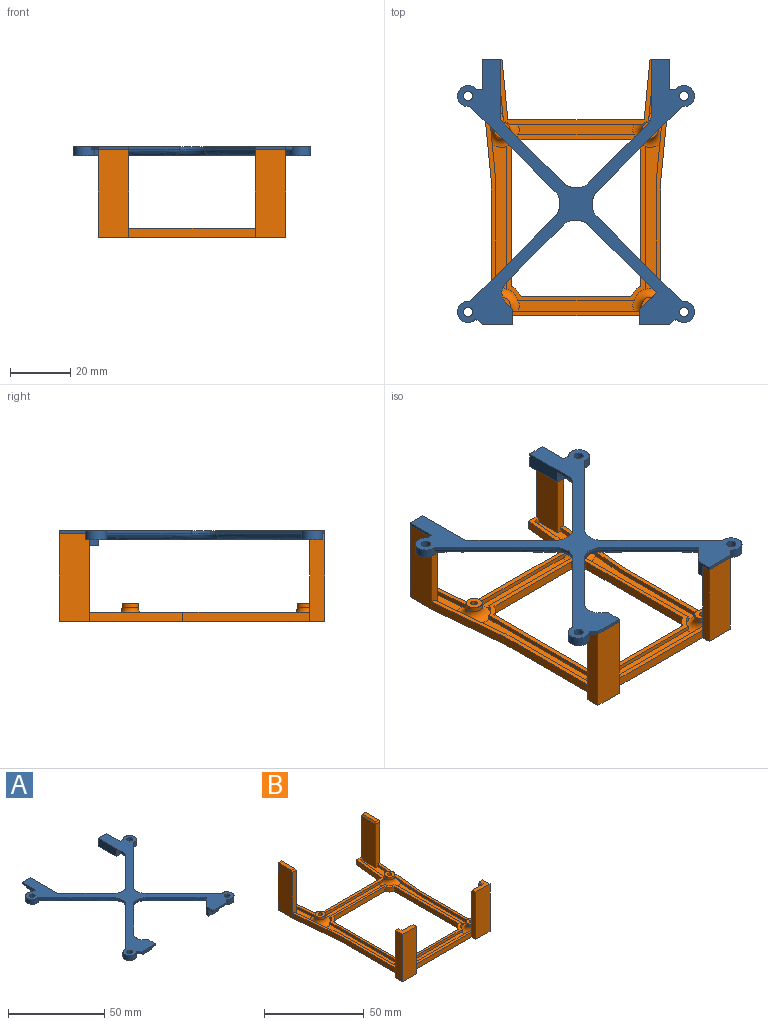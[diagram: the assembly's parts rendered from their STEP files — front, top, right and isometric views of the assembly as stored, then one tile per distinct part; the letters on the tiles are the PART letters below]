
ASSEMBLY  parts=2 mates=1
PART A: 84 faces, bbox 79.2x88.7x5.7 mm
  f0: plane 18.25x11.25mm, normal (0,0,-1), area 73.6mm2, adj f8,f9,f12,f35,f42,f60,f80
  f1: plane 14.31x14.31mm, normal (0,0,-1), area 66.3mm2, adj f6,f40,f43,f65,f66,f75,f78,f83
  f2: plane 15.43x14.79mm, normal (0,0,-1), area 66.3mm2, adj f13,f14,f15,f41,f58,f68,f69,f70
  f3: plane 11.32x11.32mm, normal (0,0,-1), area 54.9mm2, adj f71,f74,f79,f82
  f4: plane 14.25x14.25mm, normal (0,0,-1), area 83.3mm2, adj f23,f25,f26,f44,f62,f63,f73
  f5: plane 10x4mm, normal (1,0,0), area 40mm2, adj f6,f18,f55,f67
  f6: plane 5.07x5mm, normal (0,1,0), area 18.2mm2, adj f1,f5,f40,f45,f54,f55,f65,f67
  f7: plane 10x4mm, normal (-1,0,0), area 40mm2, adj f24,f25,f53,f64
  f8: plane 2.09x2.09mm, normal (0.71,-0.71,0), area 5.9mm2, adj f0,f9,f11,f51
  f9: plane 2.22x2.22mm, normal (-0.71,-0.71,0), area 6.3mm2, adj f0,f8,f12,f51
  f10: plane 7x4mm, normal (0,-1,0), area 28mm2, adj f11,f36,f51,f61
  f11: plane 4x2mm, normal (1,0,0), area 8mm2, adj f8,f10,f51,f60,f61
  f12: cylinder r=3.5mm len=7mm, axis (0,0,-1), area 52.2mm2, adj f0,f9,f37,f45,f50,f51,f80
  f13: plane 2.22x2.22mm, normal (0.71,-0.71,0), area 6.3mm2, adj f2,f14,f15,f48
  f14: plane 2.09x2.09mm, normal (-0.71,-0.71,0), area 5.9mm2, adj f2,f13,f16,f48
  f15: cylinder r=3.5mm len=7mm, axis (0,0,-1), area 52.2mm2, adj f2,f13,f29,f45,f46,f48,f69
  f16: plane 4x2mm, normal (-1,0,0), area 8mm2, adj f14,f17,f48,f58,f59
  f17: plane 7x4mm, normal (0,-1,0), area 28mm2, adj f16,f30,f48,f59
  f18: plane 6x5mm, normal (0,1,0), area 18mm2, adj f5,f19,f45,f54,f55,f67
  f19: plane 18.1x5mm, normal (-1,0,0), area 70.1mm2, adj f18,f45,f56,f66,f67,f75
  f20: plane 19.29x19.29mm, normal (-0.71,0.71,0), area 27.3mm2, adj f21,f45,f56,f81
  f21: cylinder r=6mm len=8.49mm, axis (0,0,-1), area 9.4mm2, adj f20,f22,f45,f79
  f22: plane 20.76x20.76mm, normal (0.71,0.71,0), area 29.4mm2, adj f21,f23,f45,f76
  f23: plane 23.69x5.69mm, normal (1,0,0), area 88.1mm2, adj f4,f22,f24,f45,f63,f64,f76
  f24: plane 6x5mm, normal (0,1,0), area 18mm2, adj f7,f23,f45,f52,f53,f64
  f25: plane 5.07x5mm, normal (0,1,0), area 18.2mm2, adj f4,f7,f26,f45,f52,f53,f62,f64
  f26: cylinder r=3.5mm len=7mm, axis (0,0,-1), area 46.1mm2, adj f4,f25,f27,f45,f73
  f27: plane 28.06x28.06mm, normal (-0.71,-0.71,0), area 39.7mm2, adj f26,f28,f45,f73
  f28: cylinder r=6mm len=8.49mm, axis (0,0,-1), area 9.4mm2, adj f27,f29,f45,f71
  f29: plane 28.06x28.06mm, normal (-0.71,0.71,0), area 39.7mm2, adj f15,f28,f45,f69
  f30: plane 5x5mm, normal (1,0,0), area 13mm2, adj f17,f31,f45,f47,f48,f58,f59
  f31: plane 2.05x2.05mm, normal (0.71,0.71,0), area 2.9mm2, adj f30,f45,f57,f68
  f32: plane 18.81x18.81mm, normal (0.71,-0.71,0), area 26.6mm2, adj f33,f45,f57,f72
  f33: cylinder r=6mm len=8.49mm, axis (0,0,-1), area 9.4mm2, adj f32,f34,f45,f74
  f34: plane 22.34x22.34mm, normal (-0.71,-0.71,0), area 31.6mm2, adj f33,f35,f45,f77
  f35: plane 7.33x7.33mm, normal (-0.71,0.71,0), area 24.8mm2, adj f0,f34,f36,f45,f77
  f36: plane 5x5mm, normal (-1,0,0), area 13mm2, adj f10,f35,f45,f49,f51,f60,f61
  f37: plane 28.06x28.06mm, normal (0.71,0.71,0), area 39.7mm2, adj f12,f38,f45,f80
  f38: cylinder r=6mm len=8.49mm, axis (0,0,-1), area 9.4mm2, adj f37,f39,f45,f82
  f39: plane 28.06x28.06mm, normal (0.71,-0.71,0), area 39.7mm2, adj f38,f40,f45,f83
  f40: cylinder r=3.5mm len=7mm, axis (0,0,-1), area 46.1mm2, adj f1,f6,f39,f45,f83
  f41: cylinder r=1.5mm len=3mm, axis (0,0,-1), area 28.3mm2, adj f2,f45
  f42: cylinder r=1.5mm len=3mm, axis (0,0,-1), area 28.3mm2, adj f0,f45
  f43: cylinder r=1.5mm len=3mm, axis (0,0,-1), area 28.3mm2, adj f1,f45
  f44: cylinder r=1.5mm len=3mm, axis (0,0,-1), area 28.3mm2, adj f4,f45
  f45: plane 88x78.5mm, normal (0,0,1), area 1294.3mm2, adj f6,f12,f15,f18,f19,f20,f21,f22
  f46: plane 2.14x1.92mm, normal (-0.67,-0.75,0), area 2.9mm2, adj f15,f45,f47,f48
  f47: plane 10x1mm, normal (0,-1,0), area 10mm2, adj f30,f45,f46,f48
  f48: plane 12.14x7.09mm, normal (0,0,-1), area 46.9mm2, adj f13,f14,f15,f16,f17,f30,f46,f47
  f49: plane 10x1mm, normal (0,-1,0), area 10mm2, adj f36,f45,f50,f51
  f50: plane 2.14x1.92mm, normal (0.67,-0.75,0), area 2.9mm2, adj f12,f45,f49,f51
  f51: plane 12.14x7.09mm, normal (0,0,-1), area 46.9mm2, adj f8,f9,f10,f11,f12,f36,f49,f50
  f52: plane 10x1mm, normal (-1,0,0), area 10mm2, adj f24,f25,f45,f53
  f53: plane 10x3mm, normal (0,0,-1), area 30mm2, adj f7,f24,f25,f52
  f54: plane 10x1mm, normal (1,0,0), area 10mm2, adj f6,f18,f45,f55
  f55: plane 10x3mm, normal (0,0,-1), area 30mm2, adj f5,f6,f18,f54
  f56: cylinder r=5mm len=3.54mm, axis (0,0,1), area 3.9mm2, adj f19,f20,f45,f78
  f57: cylinder r=5mm len=7.07mm, axis (0,0,1), area 7.9mm2, adj f31,f32,f45,f70
  f58: plane 7.69x4.69mm, normal (0,1,0), area 15.6mm2, adj f2,f16,f30,f59,f68
  f59: plane 7x2mm, normal (0,0,-1), area 14mm2, adj f16,f17,f30,f58
  f60: plane 7x2mm, normal (0,1,0), area 14mm2, adj f0,f11,f36,f61
  f61: plane 7x2mm, normal (0,0,-1), area 14mm2, adj f10,f11,f36,f60
  f62: plane 3x2mm, normal (-1,0,0), area 6mm2, adj f4,f25,f63,f64
  f63: plane 6x2mm, normal (0,-1,0), area 12mm2, adj f4,f23,f62,f64
  f64: plane 13x6mm, normal (0,0,-1), area 48mm2, adj f7,f23,f24,f25,f62,f63
  f65: plane 3x2mm, normal (1,0,0), area 6mm2, adj f1,f6,f66,f67
  f66: plane 6.33x4.33mm, normal (0,-1,0), area 13.1mm2, adj f1,f19,f65,f67,f75
  f67: plane 13x6mm, normal (0,0,-1), area 48mm2, adj f5,f6,f18,f19,f65,f66
  f68: bspline ~3.57x3.57mm, area 5.7mm2, adj f2,f31,f58,f70
  f69: bspline ~30.88x30.88mm, area 119.2mm2, adj f2,f15,f29,f71,f72
  f70: bspline ~9.9x3.65mm, area 27.5mm2, adj f2,f57,f68,f72
  f71: bspline ~11.31x3.97mm, area 32.3mm2, adj f3,f28,f69,f73
  f72: bspline ~20.22x20.22mm, area 80.5mm2, adj f32,f69,f70,f74
  f73: bspline ~30.88x30.88mm, area 119.2mm2, adj f4,f26,f27,f71,f76
  f74: bspline ~11.31x3.97mm, area 32.3mm2, adj f3,f33,f72,f77
  f75: bspline ~5.36x2mm, area 15.4mm2, adj f1,f19,f66,f78
  f76: bspline ~23.21x23.21mm, area 85.8mm2, adj f22,f23,f73,f79
  f77: bspline ~24.87x24.87mm, area 95.6mm2, adj f34,f35,f74,f80
  f78: bspline ~4.95x3.46mm, area 13.8mm2, adj f1,f56,f75,f81
  f79: bspline ~11.31x3.97mm, area 32.3mm2, adj f3,f21,f76,f81
  f80: bspline ~30.88x30.88mm, area 119.2mm2, adj f0,f12,f37,f77,f82
  f81: bspline ~20.9x20.9mm, area 82.6mm2, adj f20,f78,f79,f83
  f82: bspline ~11.31x3.97mm, area 32.3mm2, adj f3,f38,f80,f83
  f83: bspline ~30.88x30.88mm, area 119.2mm2, adj f1,f39,f40,f81,f82
PART B: 100 faces, bbox 66x90.1x29.1 mm
  f0: plane 74.5x4.5mm, normal (0,0,1), area 108.5mm2, adj f5,f6,f15,f16,f38,f39,f66,f88
  f1: plane 18.04x5.21mm, normal (0,0,1), area 58.8mm2, adj f18,f66,f67,f77,f90,f91
  f2: plane 45x1.5mm, normal (0,0,1), area 67.4mm2, adj f4,f6,f33,f64,f65,f79,f85,f87
  f3: plane 56x21.5mm, normal (0,0,1), area 136.1mm2, adj f8,f17,f18,f19,f41,f42,f43,f44
  f4: plane 1.2x1.05mm, normal (1,0,0), area 0.7mm2, adj f2,f6,f87
  f5: plane 1.62x1.43mm, normal (0,-1,0), area 1.5mm2, adj f0,f6,f15,f88
  f6: torus R=5.68mm, axis (0,0,1), area 65.8mm2, adj f0,f2,f4,f5,f10,f13,f15,f16
  f7: plane 74.5x4.5mm, normal (0,0,1), area 108.5mm2, adj f9,f20,f21,f47,f48,f63,f79,f82
  f8: plane 2.14x1.5mm, normal (0,-1,0), area 3.2mm2, adj f3,f12,f19,f81
  f9: plane 30.91x2.99mm, normal (1,0.1,0), area 43.4mm2, adj f7,f12,f14,f21,f78,f82
  f10: plane 48.03x4.73mm, normal (0,0,1), area 171.4mm2, adj f6,f16,f59,f66,f77
  f11: plane 38.38x3.5mm, normal (0,0,1), area 132.5mm2, adj f17,f57,f77,f78
  f12: plane 18.04x5.21mm, normal (0,0,1), area 58.8mm2, adj f8,f9,f19,f78,f81,f82
  f13: plane 38.38x3.5mm, normal (0,0,1), area 132.5mm2, adj f6,f61,f65,f79
  f14: plane 48.03x4.73mm, normal (0,0,1), area 171.4mm2, adj f9,f21,f68,f78,f79
  f15: plane 0.68x0.67mm, normal (-1,0,0), area 0.2mm2, adj f0,f5,f6
  f16: plane 38.25x1.5mm, normal (-1,0,0), area 56mm2, adj f0,f6,f10,f66
  f17: plane 44.33x1.5mm, normal (0,-1,0), area 63.7mm2, adj f3,f11,f77,f78
  f18: plane 19.04x1.92mm, normal (1,-0.1,0), area 27.4mm2, adj f1,f3,f67,f77
  f19: plane 19.04x1.92mm, normal (-1,-0.1,0), area 27.4mm2, adj f3,f8,f12,f78
  f20: plane 0.68x0.67mm, normal (1,0,0), area 0.2mm2, adj f7,f63,f79
  f21: plane 38.25x1.5mm, normal (1,0,0), area 56mm2, adj f7,f9,f14,f79
  f22: cylinder r=7mm len=3.32mm, axis (0,0,-1), area 14.4mm2, adj f23,f49,f50,f51
  f23: plane 36.35x3mm, normal (0,-1,0), area 109.1mm2, adj f22,f24,f50,f51
  f24: cylinder r=7mm len=3.32mm, axis (0,0,-1), area 14.4mm2, adj f23,f25,f50,f51
  f25: plane 45.35x3mm, normal (-1,0,0), area 136.1mm2, adj f24,f26,f50,f51
  f26: cylinder r=7mm len=3.32mm, axis (0,0,-1), area 14.4mm2, adj f25,f27,f50,f51
  f27: plane 36.35x3mm, normal (0,1,0), area 109.1mm2, adj f26,f28,f50,f51
  f28: cylinder r=7mm len=3.32mm, axis (0,0,-1), area 14.4mm2, adj f27,f49,f50,f51
  f29: plane 29x3mm, normal (0,1,0), area 86.7mm2, adj f30,f48,f51,f83,f84,f95
  f30: plane 29x5mm, normal (-1,0,0), area 145mm2, adj f29,f31,f51,f83
  f31: plane 29x10mm, normal (0,-1,0), area 290mm2, adj f30,f32,f51,f83
  f32: plane 29x3mm, normal (1,0,0), area 86.7mm2, adj f31,f33,f51,f83,f85,f94
  f33: plane 42x3mm, normal (0,-1,0), area 126mm2, adj f2,f32,f34,f51
  f34: plane 29x3mm, normal (-1,0,0), area 86.7mm2, adj f33,f35,f51,f86,f87,f98
  f35: plane 29x10mm, normal (0,-1,0), area 290mm2, adj f34,f36,f51,f86
  f36: plane 29x5mm, normal (1,0,0), area 145mm2, adj f35,f37,f51,f86
  f37: plane 29x3mm, normal (0,1,0), area 86.7mm2, adj f36,f38,f51,f86,f88,f99
  f38: plane 42.02x3mm, normal (1,0,0), area 126mm2, adj f0,f37,f39,f51
  f39: plane 30.98x3mm, normal (1,-0.1,0), area 93.4mm2, adj f0,f38,f40,f51
  f40: plane 29x10mm, normal (1,0,0), area 289.7mm2, adj f39,f41,f51,f89,f90,f93
  f41: plane 29x6.5mm, normal (0,1,0), area 97.2mm2, adj f3,f40,f42,f51,f89,f91,f92
  f42: plane 20x3mm, normal (-1,0.1,0), area 60.3mm2, adj f3,f41,f43,f51
  f43: plane 45.13x3mm, normal (0,1,0), area 135.4mm2, adj f3,f42,f44,f51
  f44: plane 20x3mm, normal (1,0.1,0), area 60.3mm2, adj f3,f43,f45,f51
  f45: plane 29x6.5mm, normal (0,1,0), area 97.2mm2, adj f3,f44,f46,f51,f80,f81,f97
  f46: plane 29x10mm, normal (-1,0,0), area 289.7mm2, adj f45,f47,f51,f80,f82,f96
  f47: plane 30.98x3mm, normal (-1,-0.1,0), area 93.4mm2, adj f7,f46,f48,f51
  f48: plane 42.02x3mm, normal (-1,0,0), area 126mm2, adj f7,f29,f47,f51
  f49: plane 45.35x3mm, normal (1,0,0), area 136.1mm2, adj f22,f28,f50,f51
  f50: plane 55x46mm, normal (0,0,1), area 282.4mm2, adj f22,f23,f24,f25,f26,f27,f28,f49
  f51: plane 88x62mm, normal (0,0,-1), area 1820.4mm2, adj f22,f23,f24,f25,f26,f27,f28,f29
  f52: cylinder r=1.07mm len=6mm, axis (0,0,-1), area 40.5mm2, adj f51,f70
  f53: cylinder r=1.07mm len=6mm, axis (0,0,-1), area 40.5mm2, adj f51,f74
  f54: cylinder r=1.07mm len=6mm, axis (0,0,-1), area 40.5mm2, adj f51,f72
  f55: cylinder r=1.07mm len=6mm, axis (0,0,-1), area 40.5mm2, adj f51,f75
  f56: cylinder r=5.5mm len=3.79mm, axis (0,0,-1), area 8.4mm2, adj f50,f57,f68,f78
  f57: plane 38.42x1.5mm, normal (0,1,0), area 57.6mm2, adj f11,f50,f56,f58,f77,f78
  f58: cylinder r=5.5mm len=3.79mm, axis (0,0,-1), area 8.4mm2, adj f50,f57,f59,f77
  f59: plane 47.42x1.5mm, normal (1,0,0), area 71.1mm2, adj f6,f10,f50,f58,f60,f77
  f60: cylinder r=5.5mm len=3.79mm, axis (0,0,-1), area 8.4mm2, adj f6,f50,f59,f61
  f61: plane 38.42x1.5mm, normal (0,-1,0), area 57.6mm2, adj f6,f13,f50,f60,f62,f79
  f62: cylinder r=5.5mm len=3.79mm, axis (0,0,-1), area 8.4mm2, adj f50,f61,f68,f79
  f63: plane 1.62x1.43mm, normal (0,-1,0), area 1.5mm2, adj f7,f20,f79,f84
  f64: plane 1.2x1.04mm, normal (-1,0,0), area 0.7mm2, adj f2,f79,f85
  f65: plane 44.33x1.5mm, normal (0,1,0), area 63.7mm2, adj f2,f6,f13,f79
  f66: plane 30.91x2.99mm, normal (-1,0.1,0), area 43.4mm2, adj f0,f1,f10,f16,f77,f90
  f67: plane 2.14x1.5mm, normal (0,-1,0), area 3.2mm2, adj f1,f3,f18,f91
  f68: plane 47.42x1.5mm, normal (-1,0,0), area 71.1mm2, adj f14,f50,f56,f62,f78,f79
  f69: cylinder r=2.67mm len=5.35mm, axis (0,0,-1), area 25.2mm2, adj f70,f79
  f70: plane 5.35x5.35mm, normal (0,0,1), area 18.8mm2, adj f52,f69
  f71: cylinder r=2.67mm len=5.35mm, axis (0,0,-1), area 25.2mm2, adj f72,f78
  f72: plane 5.35x5.35mm, normal (0,0,1), area 18.8mm2, adj f54,f71
  f73: cylinder r=2.67mm len=5.35mm, axis (0,0,-1), area 25.2mm2, adj f74,f77
  f74: plane 5.35x5.35mm, normal (0,0,1), area 18.8mm2, adj f53,f73
  f75: plane 5.35x5.35mm, normal (0,0,1), area 18.8mm2, adj f55,f76
  f76: cylinder r=2.67mm len=5.35mm, axis (0,0,-1), area 25.2mm2, adj f6,f75
  f77: torus R=5.68mm, axis (0,0,1), area 84.6mm2, adj f1,f3,f10,f11,f17,f18,f57,f58
  f78: torus R=5.68mm, axis (0,0,1), area 84.6mm2, adj f3,f9,f11,f12,f14,f17,f19,f56
  f79: torus R=5.68mm, axis (0,0,1), area 65.8mm2, adj f2,f7,f13,f14,f20,f21,f61,f62
  f80: plane 9.4x2.4mm, normal (0,0,1), area 22.6mm2, adj f45,f46,f96,f97
  f81: plane 26.5x10mm, normal (1,0,0), area 262.8mm2, adj f3,f8,f12,f45,f82,f97
  f82: plane 26.5x3mm, normal (0,-1,0), area 77.2mm2, adj f7,f9,f12,f46,f81,f96
  f83: plane 10x5mm, normal (0,0,1), area 30.2mm2, adj f29,f30,f31,f32,f94,f95
  f84: plane 26.42x2.01mm, normal (1,0,0), area 50.7mm2, adj f7,f29,f63,f79,f85,f95
  f85: plane 26.42x7.01mm, normal (0,1,0), area 179.8mm2, adj f2,f32,f64,f79,f84,f94
  f86: plane 10x5mm, normal (0,0,1), area 30.2mm2, adj f34,f35,f36,f37,f98,f99
  f87: plane 26.42x7.01mm, normal (0,1,0), area 179.8mm2, adj f2,f4,f6,f34,f88,f98
  f88: plane 26.42x2.01mm, normal (-1,0,0), area 50.7mm2, adj f0,f5,f6,f37,f87,f99
  f89: plane 9.4x2.4mm, normal (0,0,1), area 22.6mm2, adj f40,f41,f92,f93
  f90: plane 26.5x3mm, normal (0,-1,0), area 77.2mm2, adj f0,f1,f40,f66,f91,f93
  f91: plane 26.5x10mm, normal (-1,0,0), area 262.8mm2, adj f1,f3,f41,f67,f90,f92
  f92: plane 10x1mm, normal (-0.86,0,0.51), area 11.3mm2, adj f41,f89,f91,f93
  f93: plane 3x1mm, normal (0,-0.86,0.51), area 3.1mm2, adj f40,f89,f90,f92
  f94: plane 7.6x1mm, normal (0,0.86,0.51), area 8.5mm2, adj f32,f83,f85,f95
  f95: plane 2.6x1mm, normal (0.86,0,0.51), area 2.7mm2, adj f29,f83,f84,f94
  f96: plane 3x1mm, normal (0,-0.86,0.51), area 3.1mm2, adj f46,f80,f82,f97
  f97: plane 10x1mm, normal (0.86,0,0.51), area 11.3mm2, adj f45,f80,f81,f96
  f98: plane 7.6x1mm, normal (0,0.86,0.51), area 8.5mm2, adj f34,f86,f87,f99
  f99: plane 2.6x1mm, normal (-0.86,0,0.51), area 2.7mm2, adj f37,f86,f88,f98
PLACE A t=(0,4.02,24)mm
PLACE B t=(0,4.02,0)mm
MATE fastened B.f83 <-> A.f48  axis (0,0,1) through (-21,-41.48,29)mm
